# Revit family: SW18 SKYGGE
name_source: partatom
category: Detail Items
units: mm (PartAtom-declared; Revit-internal decimal feet)

## family parameters
Rotate with component = No
Section Shape = Not Defined
Shared = No

## types (5) — shared parameters
URL = www.superwood.dk

## per-type parameters (varying)
| type | Bredde | Skulder afstand 1 | Skulder afstand 2 | h |
| SW18 SKYGGE 4" - 27x95mm | 27 mm | 17 mm | 13 mm | 95 mm |
| SW18 SKYGGE 6" - 21x145mm | 21 mm  [stored 0.0688976 ft] | 19 mm  [stored 0.062336 ft] | 15 mm  [stored 0.0492126 ft] | 145 mm  [stored 0.475722 ft] |
| SW18 SKYGGE 5" - 21x120mm | 21 mm  [stored 0.0688976 ft] | 19 mm  [stored 0.062336 ft] | 15 mm  [stored 0.0492126 ft] | 120 mm |
| SW18 SKYGGE 4" - 21x95mm | 21 mm  [stored 0.0688976 ft] | 17 mm | 13 mm | 95 mm |
| SW18 SKYGGE 3" - 21x70mm | 21 mm  [stored 0.0688976 ft] | 17 mm | 13 mm | 70 mm |

note: [stored X ft] marks values corroborated as IEEE doubles in the binary element streams (Revit-internal decimal feet)

## geometry (parser evidence)
native form markers: Sweep x2
no freeform markers — native parametric forms only
